# Revit family: CMH-WM250V-A
name_source: partatom
category: Mechanical Equipment
revit_build: Autodesk Revit 2016 (Build: 20150220_1215(x64)
units: mm (PartAtom-declared; Revit-internal decimal feet)

## family parameters
Always vertical = Yes
Cut with Voids When Loaded = No
OmniClass Number = 23.75.00.00
OmniClass Title = Climate Control (HVAC)
Part Type = Normal
Room Calculation Point = No
Round Connector Dimension = Use Radius
Shared = No
Work Plane-Based = No

## types (24) — shared parameters
Applicable temperature range of installation site = -5 to 52
Connectable Outdoor/Heat source Unit = PUHY-M200 to 250YNW-A1(-BS)/PUHY-EM200 to 250YNW-A1(-BS)
Cooling Power Input (kW) = 0.74
Depth = 740 mm  [stored 2.42782 ft]
Description = Hydro unit
External Finish = Pre-coated galvanized steel sheets
Gas pipe_radius = 11.1 mm  [stored 0.0364173 ft]
Heating Power Input (kW) = 0.74
Height = 660 mm
Liquid pipe_radius = 4.76 mm
Manufacturer = Mitsubishi Electric Corporation
Model = CMH-WM250V-A
Phase = 1
Sound Pressure Level (dB(A)) = 60
Space View = Yes
Subcategory = HVAC
URL = http://www.mitsubishielectric.com
Unit Weight (kg) = 125
Water Pipe radius (EXP. Vessel) = 11 mm  [stored 0.0360892 ft]
Water Pipe radius (From Indoor Unit) = 20 mm  [stored 0.0656168 ft]
Water Pipe radius (Inlet) = 11 mm  [stored 0.0360892 ft]
Water Pipe radius (To Indoor Unit) = 20 mm  [stored 0.0656168 ft]
Width = 920 mm  [stored 3.01837 ft]
zero-valued in all types: Equip_No., SerialNumber, TagNumber

## per-type parameters (varying)
| type | Cooling Current (A) | Heating Current (A) | Hertz | Voltage |
| CMH-WM250V-A_220V_50Hz_To M200 | 3.84 | 3.84 | 50 Hz | 220 V |
| CMH-WM250V-A_220V_60Hz_To M200 | 3.67 | 3.67 | 60 Hz | 220 V |
| CMH-WM250V-A_230V_50Hz_To M200 | 3.84 | 3.84 | 50 Hz | 230 V |
| CMH-WM250V-A_230V_60Hz_To M200 | 3.67 | 3.67 | 60 Hz | 230 V |
| CMH-WM250V-A_240V_50Hz_To M200 | 3.52 | 3.52 | 50 Hz | 240 V |
| CMH-WM250V-A_240V_60Hz_To M200 | 3.52 | 3.52 | 60 Hz | 240 V |
| CMH-WM250V-A_220V_50Hz_To M250 | 3.84 | 3.84 | 50 Hz | 220 V |
| CMH-WM250V-A_220V_60Hz_To M250 | 3.84 | 3.84 | 60 Hz | 220 V |
| CMH-WM250V-A_230V_50Hz_To M250 | 3.67 | 3.67 | 50 Hz | 230 V |
| CMH-WM250V-A_230V_60Hz_To M250 | 3.67 | 3.67 | 60 Hz | 230 V |
| CMH-WM250V-A_240V_50Hz_To M250 | 3.52 | 3.52 | 50 Hz | 240 V |
| CMH-WM250V-A_240V_60Hz_To M250 | 3.52 | 3.52 | 60 Hz | 240 V |
| CMH-WM250V-A_220V_50Hz_To EM200 | 3.84 | 3.84 | 50 Hz | 220 V |
| CMH-WM250V-A_220V_60Hz_To EM200 | 3.84 | 3.84 | 60 Hz | 220 V |
| CMH-WM250V-A_230V_50Hz_To EM200 | 3.67 | 3.67 | 50 Hz | 230 V |
| CMH-WM250V-A_230V_60Hz_To EM200 | 3.67 | 3.67 | 60 Hz | 230 V |
| CMH-WM250V-A_240V_50Hz_To EM200 | 3.52 | 3.52 | 50 Hz | 240 V |
| CMH-WM250V-A_240V_60Hz_To EM200 | 3.52 | 3.52 | 60 Hz | 240 V |
| CMH-WM250V-A_220V_50Hz_To EM250 | 3.84 | 3.84 | 50 Hz | 220 V |
| CMH-WM250V-A_220V_60Hz_To EM250 | 3.84 | 3.84 | 60 Hz | 220 V |
| CMH-WM250V-A_230V_50Hz_To EM250 | 3.67 | 3.67 | 50 Hz | 230 V |
| CMH-WM250V-A_230V_60Hz_To EM250 | 3.67 | 3.67 | 60 Hz | 230 V |
| CMH-WM250V-A_240V_50Hz_To EM250 | 3.52 | 3.52 | 50 Hz | 240 V |
| CMH-WM250V-A_240V_60Hz_To EM250 | 3.52 | 3.52 | 60 Hz | 240 V |

note: [stored X ft] marks values corroborated as IEEE doubles in the binary element streams (Revit-internal decimal feet)

## geometry (parser evidence)
native form markers: Blend x40, Sweep x1
no freeform markers — native parametric forms only
